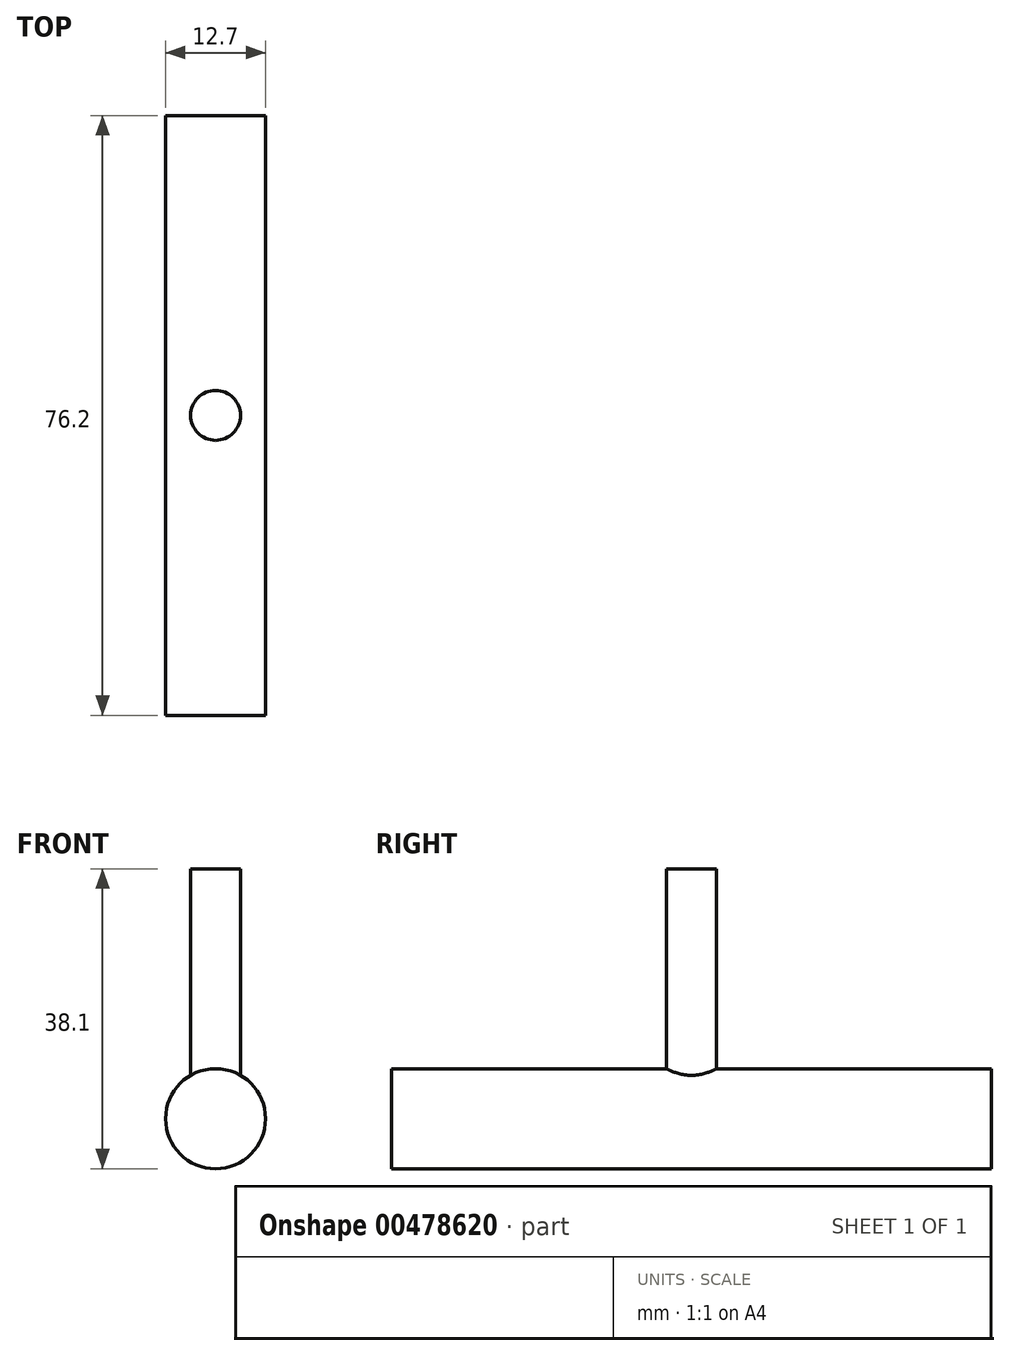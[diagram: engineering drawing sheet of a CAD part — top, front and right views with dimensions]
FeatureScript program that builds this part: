
annotation { "Feature Type Name" : "Feature", "Feature Type Description" : "" }
export const myFeature = defineFeature(function(context is Context, id is Id, definition is map)
    precondition{}
    {
        {
            var Q0;
            Q0=qCreatedBy(makeId("Front.planeOp"),FACE);
            var sketch = newSketch(context, id + "F0", { "sketchPlane" : qUnion([Q0])});
            skCircle(sketch, "E0", {"center": v(0, 0) * mm, "radius": 6.35 * mm});
            skSolve(sketch);
        }
        {
            var Q0;
            Q0=qCreatedBy(makeId("Top.planeOp"),FACE);
            var sketch = newSketch(context, id + "F1", { "sketchPlane" : qUnion([Q0])});
            skCircle(sketch, "E1", {"center": v(0, 0) * mm, "radius": 3.18 * mm});
            skSolve(sketch);
        }
        {
            var Q0;
            Q0=makeQuery(id+"F1.imprint","IMPRINT",FACE,{"disambiguationData":[TD([[makeQuery(id+"F1.imprint","IMPRINT",EDGE,{"derivedFrom":sQuery(id+"F1.wireOp",EDGE,"E1")}),1.0]])]});
            extrude(context, id + "F2", {"entities" : qUnion([Q0]), "depth" : 31.75 * mm});
        }
        {
            var Q0;
            Q0=makeQuery(id+"F0.imprint","IMPRINT",FACE,{"disambiguationData":[TD([[makeQuery(id+"F0.imprint","IMPRINT",EDGE,{"derivedFrom":sQuery(id+"F0.wireOp",EDGE,"E0")}),1.0]])]});
            extrude(context, id + "F3", {"entities" : qUnion([Q0]), "operationType" : NewBodyOperationType.ADD, "depth" : 38.1 * mm});
        }
        {
            var Q0;
            Q0 = qSketchRegion(id + "F0", true);
            extrude(context, id + "F4", {"entities" : qUnion([Q0]), "operationType" : NewBodyOperationType.ADD, "oppositeDirection" : true, "depth" : 38.1 * mm});
        }
    });
